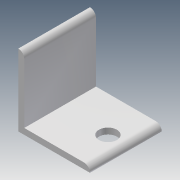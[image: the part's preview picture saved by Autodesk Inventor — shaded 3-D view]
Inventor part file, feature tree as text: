
AUTODESK INVENTOR PART (.ipt)
format: ipt  version: 2014 (Build 180170000, 170)  size: 89,088 bytes
history: native  units: in
note: dims shown in document units (in); Inventor stores cm internally (conversion verified against a paired STEP export)
features: extrude x2, sketch x2
ambient origin geometry x8: Origin, YZ Plane, XZ Plane, XY Plane, X Axis, Y Axis, Z Axis, Center Point
bodies: Solid1 (feature_tree)
feature tree (4):
  extrude  "Extrusion1"  Depth=1.5in
  extrude  "Extrusion2"  Depth=1.5in TaperAngle=0.0deg
  sketch  "Sketch1"  dims[d0=1.5in d1=1.5in]
  sketch  "Sketch2"  dims[d2=0.125in d3=1.5in d4=0.0in d5=0.375in d6=0.375in d7=1.5in d8=0.0in]
